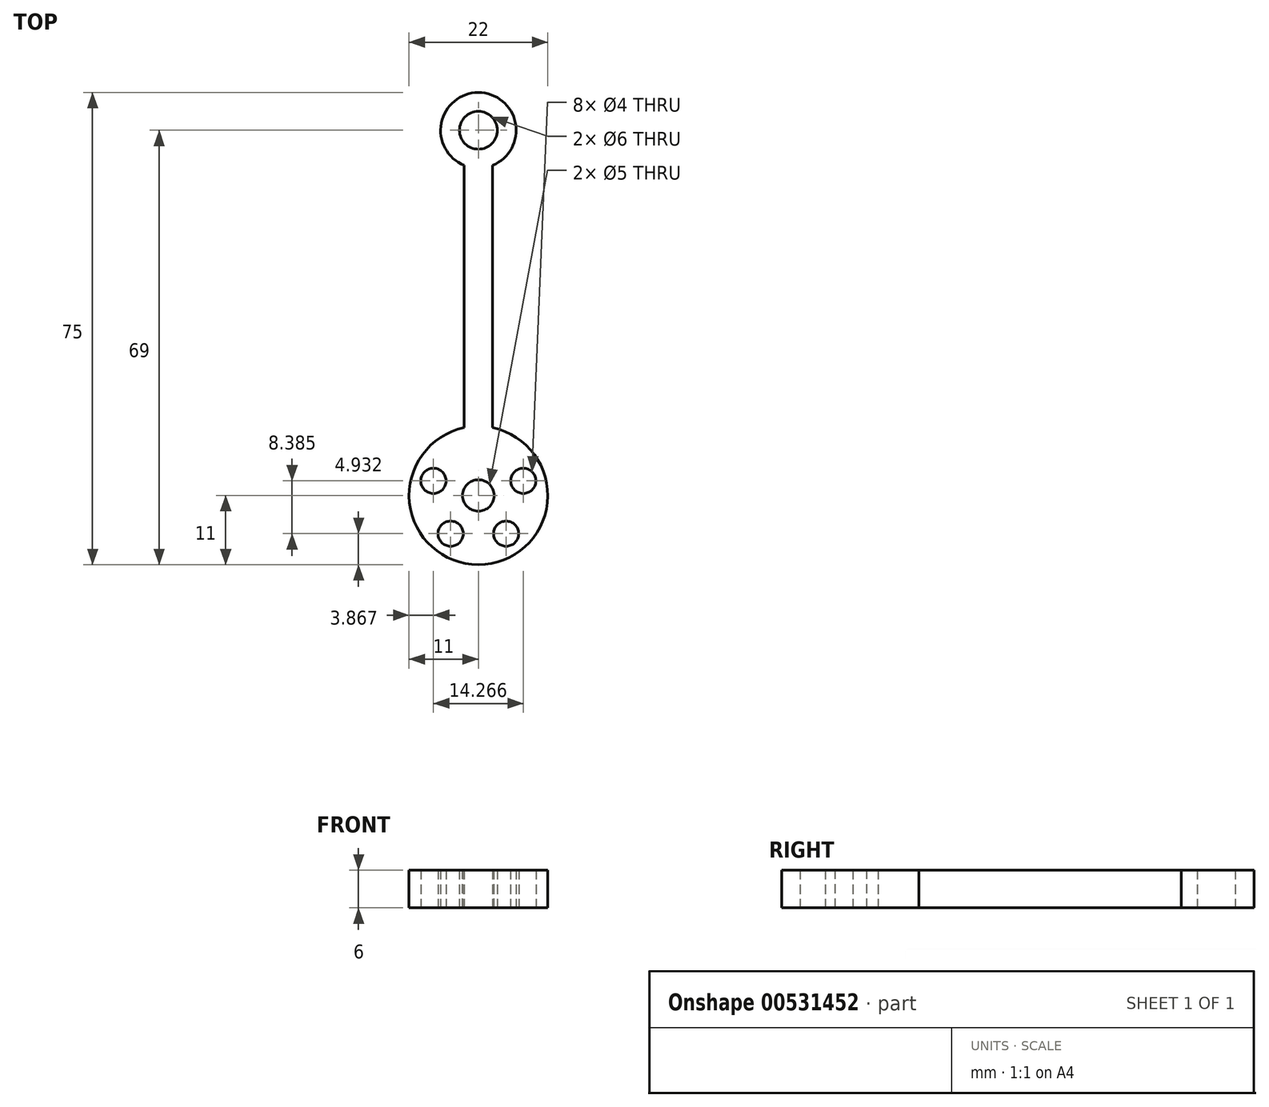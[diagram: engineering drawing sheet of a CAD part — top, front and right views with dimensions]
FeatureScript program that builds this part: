
annotation { "Feature Type Name" : "Feature", "Feature Type Description" : "" }
export const myFeature = defineFeature(function(context is Context, id is Id, definition is map)
    precondition{}
    {
        {
            var Q0;
            Q0=qCreatedBy(makeId("Top.planeOp"),FACE);
            var sketch = newSketch(context, id + "F0", { "sketchPlane" : qUnion([Q0])});
            skArc(sketch, "E0", {"start": v(-2.25, 10.77) * mm, "mid": v(0, -11) * mm, "end": v(2.25, 10.77) * mm});
            skArc(sketch, "E1", {"start": v(2.25, 52.44) * mm, "mid": v(0, 64) * mm, "end": v(-2.25, 52.44) * mm});
            skLineSegment(sketch, "E2", {"start": v(-2.25, 52.44) * mm, "end": v(-2.25, 10.77) * mm});
            skLineSegment(sketch, "E3", {"start": v(2.25, 52.44) * mm, "end": v(2.25, 10.77) * mm});
            skCircle(sketch, "E4", {"center": v(0, 58) * mm, "radius": 3 * mm});
            skCircle(sketch, "E5.cCircle", {"center": v(0, 0) * mm, "radius": 7.5 * mm, "construction": true});
            skLineSegment(sketch, "E5.0", {"start": v(0, 7.5) * mm, "end": v(7.13, 2.32) * mm, "construction": true});
            skLineSegment(sketch, "E5.1", {"start": v(7.13, 2.32) * mm, "end": v(4.4, -6.07) * mm, "construction": true});
            skLineSegment(sketch, "E5.2", {"start": v(4.4, -6.07) * mm, "end": v(-4.4, -6.07) * mm, "construction": true});
            skLineSegment(sketch, "E5.3", {"start": v(-4.4, -6.07) * mm, "end": v(-7.13, 2.32) * mm, "construction": true});
            skLineSegment(sketch, "E5.4", {"start": v(-7.13, 2.32) * mm, "end": v(0, 7.5) * mm, "construction": true});
            skCircle(sketch, "E6", {"center": v(-7.13, 2.32) * mm, "radius": 2 * mm});
            skCircle(sketch, "E7", {"center": v(-4.4, -6.07) * mm, "radius": 2 * mm});
            skCircle(sketch, "E8", {"center": v(4.4, -6.07) * mm, "radius": 2 * mm});
            skCircle(sketch, "E9", {"center": v(7.13, 2.32) * mm, "radius": 2 * mm});
            skSolve(sketch);
        }
        {
            var Q0;
            Q0 = qSketchRegion(id + "F0", true);
            extrude(context, id + "F1", {"entities" : qUnion([Q0]), "depth" : 6 * mm, "offsetDistance" : 25 * mm});
        }
        {
            var Q0;
            Q0=makeQuery(id+"F1.opExtrude","CAP_FACE",FACE,{"disambiguationData":[OSD([sQuery(id+"F0.wireOp",EDGE,"E0"),sQuery(id+"F0.wireOp",EDGE,"E1"),sQuery(id+"F0.wireOp",EDGE,"E2"),sQuery(id+"F0.wireOp",EDGE,"E3"),sQuery(id+"F0.wireOp",EDGE,"E4"),sQuery(id+"F0.wireOp",EDGE,"E6"),sQuery(id+"F0.wireOp",EDGE,"E7"),sQuery(id+"F0.wireOp",EDGE,"E8"),sQuery(id+"F0.wireOp",EDGE,"E9")])],"isStart":false});
            var sketch = newSketch(context, id + "F2", { "sketchPlane" : qUnion([Q0])});
            skCircle(sketch, "E10", {"center": v(0, 0) * mm, "radius": 2.5 * mm});
            skSolve(sketch);
        }
        {
            var Q0;
            Q0 = qSketchRegion(id + "F2", true);
            extrude(context, id + "F3", {"entities" : qUnion([Q0]), "operationType" : NewBodyOperationType.REMOVE, "oppositeDirection" : true, "depth" : 8.1 * mm, "offsetDistance" : 25 * mm});
        }
    });
